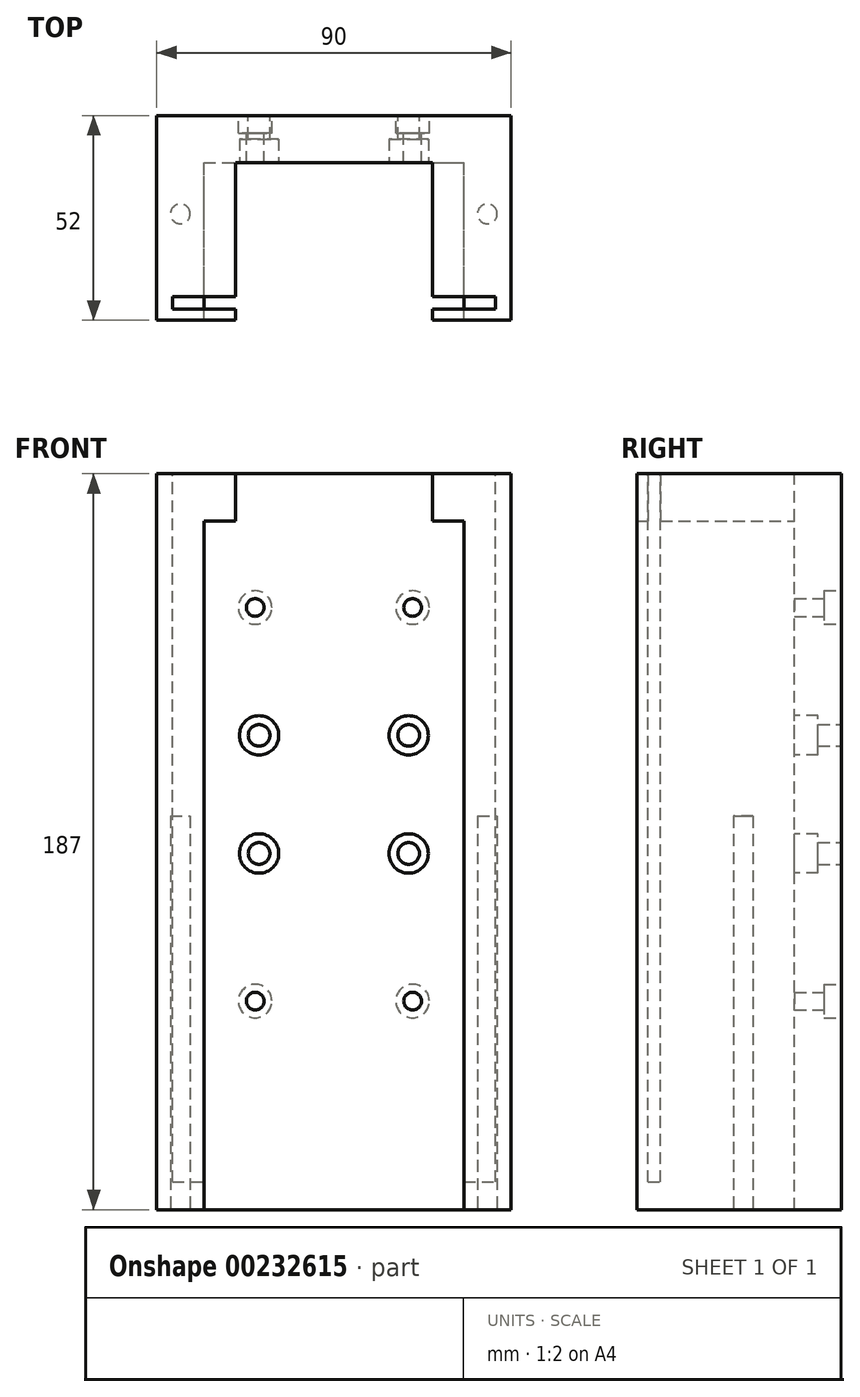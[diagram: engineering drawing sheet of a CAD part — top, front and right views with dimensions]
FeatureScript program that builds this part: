
annotation { "Feature Type Name" : "Feature", "Feature Type Description" : "" }
export const myFeature = defineFeature(function(context is Context, id is Id, definition is map)
    precondition{}
    {
        {
            var Q0;
            Q0=qCreatedBy(makeId("Front.planeOp"),FACE);
            var sketch = newSketch(context, id + "F0", { "sketchPlane" : qUnion([Q0])});
            skLineSegment(sketch, "E0.bottom", {"start": v(0, 0) * mm, "end": v(90, 0) * mm});
            skLineSegment(sketch, "E0.top", {"start": v(0, 187) * mm, "end": v(90, 187) * mm});
            skLineSegment(sketch, "E0.left", {"start": v(0, 0) * mm, "end": v(0, 187) * mm});
            skLineSegment(sketch, "E0.right", {"start": v(90, 0) * mm, "end": v(90, 187) * mm});
            skSolve(sketch);
        }
        {
            var Q0;
            Q0=makeQuery(id+"F0.imprint","IMPRINT",FACE,{"disambiguationData":[TD([[makeQuery(id+"F0.imprint","IMPRINT",EDGE,{"derivedFrom":sQuery(id+"F0.wireOp",EDGE,"E0.bottom")}),1.0]])]});
            extrude(context, id + "F1", {"entities" : qUnion([Q0]), "depth" : 52 * mm});
        }
        {
            var Q0;
            Q0=makeQuery(id+"F1.opExtrude","CAP_FACE",FACE,{"disambiguationData":[OSD([sQuery(id+"F0.wireOp",EDGE,"E0.bottom"),sQuery(id+"F0.wireOp",EDGE,"E0.top"),sQuery(id+"F0.wireOp",EDGE,"E0.left"),sQuery(id+"F0.wireOp",EDGE,"E0.right")])],"isStart":false});
            var Q1;
            Q1=makeQuery(id+"F1.opExtrude","SWEPT_FACE",FACE,{"disambiguationData":[OSD([sQuery(id+"F0.wireOp",EDGE,"E0.bottom")])]});
            shell(context, id + "F2", {"entities" : qUnion([Q0, Q1]), "thickness" : 12 * mm});
        }
        {
            var Q0;
            Q0=makeQuery(id+"F1.opExtrude","SWEPT_FACE",FACE,{"disambiguationData":[OSD([sQuery(id+"F0.wireOp",EDGE,"E0.top")])]});
            var sketch = newSketch(context, id + "F3", { "sketchPlane" : qUnion([Q0])});
            skLineSegment(sketch, "E1.bottom", {"start": v(20, -52) * mm, "end": v(70, -52) * mm});
            skLineSegment(sketch, "E1.top", {"start": v(20, -12) * mm, "end": v(70, -12) * mm});
            skLineSegment(sketch, "E1.left", {"start": v(20, -52) * mm, "end": v(20, -12) * mm});
            skLineSegment(sketch, "E1.right", {"start": v(70, -52) * mm, "end": v(70, -12) * mm});
            skSolve(sketch);
        }
        {
            var Q0;
            Q0 = qSketchRegion(id + "F3", true);
            extrude(context, id + "F4", {"entities" : qUnion([Q0]), "operationType" : NewBodyOperationType.REMOVE, "oppositeDirection" : true, "depth" : 25 * mm});
        }
        {
            var Q0;
            Q0=makeQuery(id+"F1.opExtrude","CAP_FACE",FACE,{"disambiguationData":[OSD([sQuery(id+"F0.wireOp",EDGE,"E0.bottom"),sQuery(id+"F0.wireOp",EDGE,"E0.top"),sQuery(id+"F0.wireOp",EDGE,"E0.left"),sQuery(id+"F0.wireOp",EDGE,"E0.right")])],"isStart":true});
            var sketch = newSketch(context, id + "F5", { "sketchPlane" : qUnion([Q0])});
            skCircle(sketch, "E2", {"center": v(-65, 53) * mm, "radius": 2.25 * mm});
            skCircle(sketch, "E3", {"center": v(-25, 53) * mm, "radius": 2.25 * mm});
            skCircle(sketch, "E4", {"center": v(-65, 153) * mm, "radius": 2.25 * mm});
            skCircle(sketch, "E5", {"center": v(-25, 153) * mm, "radius": 2.25 * mm});
            skCircle(sketch, "E6", {"center": v(-26, 120.5) * mm, "radius": 2.75 * mm});
            skCircle(sketch, "E7", {"center": v(-64, 120.5) * mm, "radius": 2.75 * mm});
            skCircle(sketch, "E8", {"center": v(-26, 90.5) * mm, "radius": 2.75 * mm});
            skCircle(sketch, "E9", {"center": v(-64, 90.5) * mm, "radius": 2.75 * mm});
            skSolve(sketch);
        }
        {
            var Q0;
            Q0 = qSketchRegion(id + "F5", true);
            extrude(context, id + "F6", {"entities" : qUnion([Q0]), "operationType" : NewBodyOperationType.REMOVE, "endBound" : BoundingType.THROUGH_ALL, "oppositeDirection" : true, "depth" : 25 * mm});
        }
        {
            var Q0;
            Q0=makeQuery(id+"F2.opShell","OFFSET_FACE",FACE,{"disambiguationData":[OSD([sQuery(id+"F0.wireOp",EDGE,"E0.bottom"),sQuery(id+"F0.wireOp",EDGE,"E0.top"),sQuery(id+"F0.wireOp",EDGE,"E0.left"),sQuery(id+"F0.wireOp",EDGE,"E0.right")])]});
            var sketch = newSketch(context, id + "F7", { "sketchPlane" : qUnion([Q0])});
            skCircle(sketch, "E10", {"center": v(26, 120.5) * mm, "radius": 5 * mm});
            skCircle(sketch, "E11", {"center": v(64, 120.5) * mm, "radius": 5 * mm});
            skCircle(sketch, "E12", {"center": v(26, 90.5) * mm, "radius": 5 * mm});
            skCircle(sketch, "E13", {"center": v(64, 90.5) * mm, "radius": 5 * mm});
            skSolve(sketch);
        }
        {
            var Q0;
            Q0 = qSketchRegion(id + "F7", true);
            extrude(context, id + "F8", {"entities" : qUnion([Q0]), "operationType" : NewBodyOperationType.REMOVE, "oppositeDirection" : true, "depth" : 6 * mm});
        }
        {
            var Q0;
            Q0=makeQuery(id+"F1.opExtrude","CAP_FACE",FACE,{"disambiguationData":[OSD([sQuery(id+"F0.wireOp",EDGE,"E0.bottom"),sQuery(id+"F0.wireOp",EDGE,"E0.top"),sQuery(id+"F0.wireOp",EDGE,"E0.left"),sQuery(id+"F0.wireOp",EDGE,"E0.right")])],"isStart":true});
            var sketch = newSketch(context, id + "F9", { "sketchPlane" : qUnion([Q0])});
            skCircle(sketch, "E14", {"center": v(-65, 153) * mm, "radius": 4.25 * mm});
            skCircle(sketch, "E15", {"center": v(-25, 153) * mm, "radius": 4.25 * mm});
            skCircle(sketch, "E16", {"center": v(-65, 53) * mm, "radius": 4.25 * mm});
            skCircle(sketch, "E17", {"center": v(-25, 53) * mm, "radius": 4.25 * mm});
            skSolve(sketch);
        }
        {
            var Q0;
            Q0 = qSketchRegion(id + "F9", true);
            extrude(context, id + "F10", {"entities" : qUnion([Q0]), "operationType" : NewBodyOperationType.REMOVE, "oppositeDirection" : true, "depth" : 4.5 * mm});
        }
        {
            var Q0;
            Q0=makeQuery(id+"F1.opExtrude","SWEPT_FACE",FACE,{"disambiguationData":[OSD([sQuery(id+"F0.wireOp",EDGE,"E0.bottom")])]});
            var sketch = newSketch(context, id + "F11", { "sketchPlane" : qUnion([Q0])});
            skCircle(sketch, "E18", {"center": v(6, 25) * mm, "radius": 2.5 * mm});
            skCircle(sketch, "E19", {"center": v(84, 25) * mm, "radius": 2.5 * mm});
            skSolve(sketch);
        }
        {
            var Q0;
            Q0 = qSketchRegion(id + "F11", true);
            extrude(context, id + "F12", {"entities" : qUnion([Q0]), "operationType" : NewBodyOperationType.REMOVE, "oppositeDirection" : true, "depth" : 100 * mm});
        }
        {
            var Q0;
            Q0=makeQuery(id+"F1.opExtrude","SWEPT_FACE",FACE,{"disambiguationData":[OSD([sQuery(id+"F0.wireOp",EDGE,"E0.top")])]});
            var sketch = newSketch(context, id + "F13", { "sketchPlane" : qUnion([Q0])});
            skLineSegment(sketch, "E20.bottom", {"start": v(4, -46) * mm, "end": v(86, -46) * mm});
            skLineSegment(sketch, "E20.top", {"start": v(4, -49.25) * mm, "end": v(86, -49.25) * mm});
            skLineSegment(sketch, "E20.left", {"start": v(4, -46) * mm, "end": v(4, -49.25) * mm});
            skLineSegment(sketch, "E20.right", {"start": v(86, -46) * mm, "end": v(86, -49.25) * mm});
            skSolve(sketch);
        }
        {
            var Q0;
            Q0 = qSketchRegion(id + "F13", true);
            extrude(context, id + "F14", {"entities" : qUnion([Q0]), "operationType" : NewBodyOperationType.REMOVE, "oppositeDirection" : true, "depth" : 180 * mm});
        }
    });
